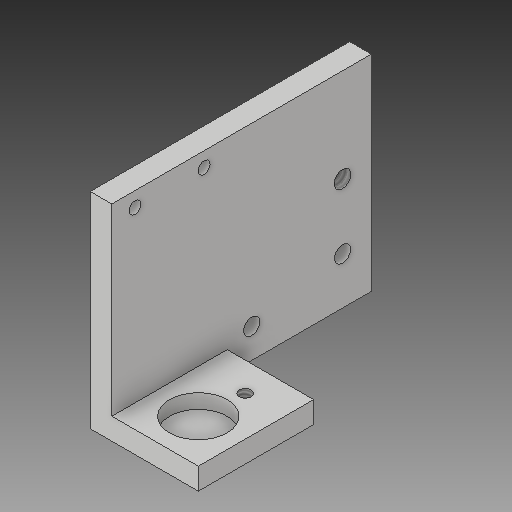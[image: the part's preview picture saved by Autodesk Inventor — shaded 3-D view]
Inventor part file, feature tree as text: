
AUTODESK INVENTOR PART (.ipt)
format: ipt  version: 2017 (Build 210142000, 142)  size: 175,104 bytes
history: native  units: in
note: dims shown in document units (in); Inventor stores cm internally (conversion verified against a paired STEP export)
features: sketch x8, projected_geometry x7, hole x6, extrude x3
ambient origin geometry x8: Origin, YZ Plane, XZ Plane, XY Plane, X Axis, Y Axis, Z Axis, Center Point
bodies: Solid1 (feature_tree)
feature tree (24):
  extrude  "Extrusion1"  Depth=2.25in
  extrude  "Extrusion3"  Depth=0.1875in
  extrude  "Extrusion4"  Depth=0.3125in TaperAngle=0.0deg
  hole  "Hole1"  [1 undecoded]
  hole  "Hole2"  [1 undecoded]
  hole  "Hole3"  [1 undecoded]
  hole  "Hole4"  [1 undecoded]
  hole  "Hole5"  [1 undecoded]
  hole  "Hole6"  [1 undecoded]
  sketch  "Sketch1"  dims[d0=1.7812in d1=2.25in]
  sketch  "Sketch3"  dims[d2=0.1875in d3=0.0in d8=0.1875in]
  projected_geometry  "Projected Loop2"
  projected_geometry  "Projected Loop3"
  sketch  "Sketch5"  dims[d9=0.75in d10=0.0in d13=0.3125in d14=0.0in]
  projected_geometry  "Projected Loop4"
  sketch  "Sketch6"  dims[d15=0.1875in d16=0.8125in d17=0.25in]
  projected_geometry  "Projected Loop6"
  sketch  "Sketch10"  dims[d18=0.145in d19=0.38in d20=0.375in d21=0.25in d22=0.5635in d23=0.588in d24=0.8108in d25=0.375in]
  projected_geometry  "Projected Loop10"
  sketch  "Sketch11"  dims[d26=0.375in]
  projected_geometry  "Projected Loop11"
  sketch  "Sketch12"  dims[d27=0.5in d28=0.75in d29=0.375in d30=0.25in d31=0.5635in d32=0.125in d33=0.0in d48=0.625in]
  projected_geometry  "Projected Loop12"
  sketch  "Sketch13"  dims[d49=0.5in d50=0.5in d51=0.104in d52=0.276in d53=0.375in d54=0.25in d55=0.5635in d56=0.432in d57=0.8108in d58=0.25in d59=0.104in d60=0.276in d61=0.375in d62=0.25in d63=0.5635in d64=0.432in d65=0.8108in d66=0.25in d67=0.406in d68=0.256in d69=1.0375in d70=0.14in d71=0.75in d72=0.375in d73=0.25in d74=0.5635in d75=1.0in d76=0.8108in d77=0.2in d78=0.6in d79=0.104in d80=0.75in d81=0.375in d82=0.25in d83=0.5635in d84=1.0in d85=0.8108in]
note: 6 required parameter values undecoded (feature->parameter linkage not recoverable at this tier; creation-order binding heuristic only, values carry confidence <= 0.55)
